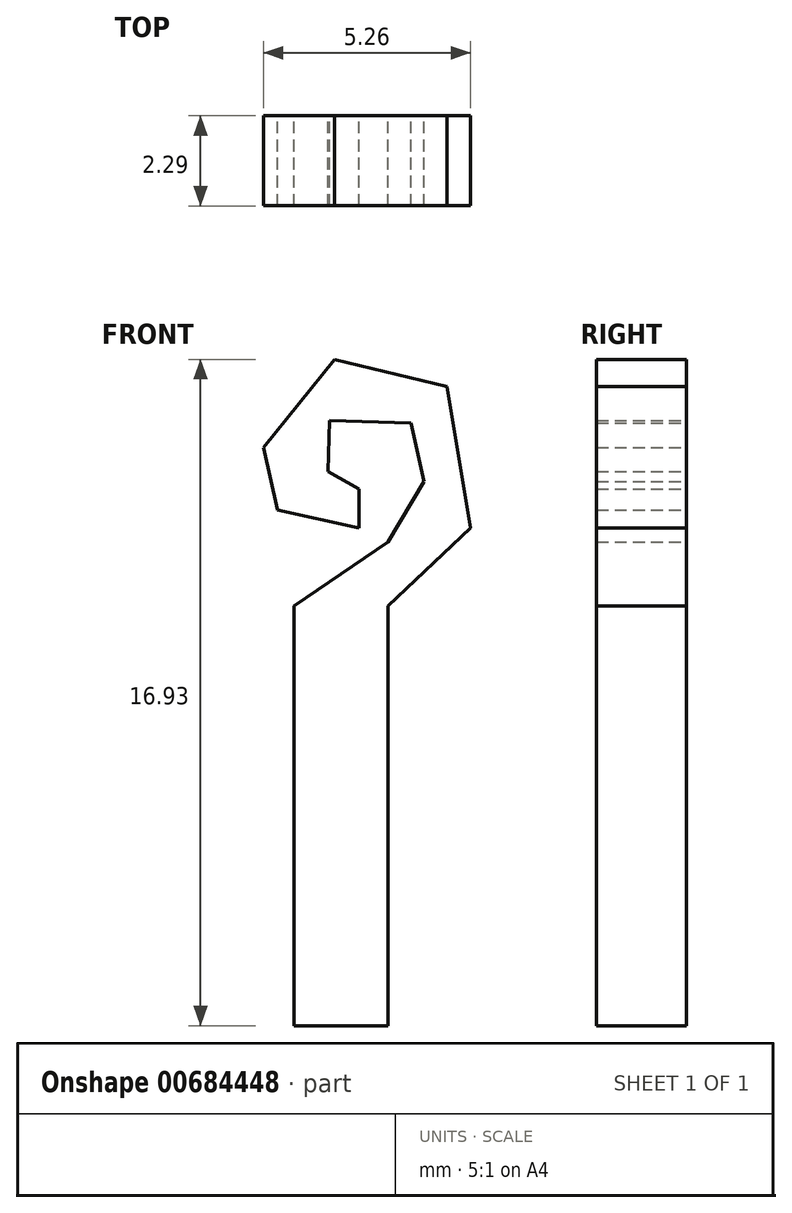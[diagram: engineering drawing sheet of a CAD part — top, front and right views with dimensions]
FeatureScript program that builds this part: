
annotation { "Feature Type Name" : "Feature", "Feature Type Description" : "" }
export const myFeature = defineFeature(function(context is Context, id is Id, definition is map)
    precondition{}
    {
        {
            var Q0;
            Q0=qCreatedBy(makeId("Front.planeOp"),FACE);
            var sketch = newSketch(context, id + "F0", { "sketchPlane" : qUnion([Q0])});
            skLineSegment(sketch, "E0", {"start": v(0, 0) * mm, "end": v(0, 10.67) * mm});
            skLineSegment(sketch, "E1", {"start": v(0, 0) * mm, "end": v(2.39, 0) * mm});
            skLineSegment(sketch, "E2", {"start": v(2.39, 0) * mm, "end": v(2.39, 10.67) * mm});
            skLineSegment(sketch, "E3", {"start": v(2.39, 10.67) * mm, "end": v(4.49, 12.65) * mm});
            skLineSegment(sketch, "E4", {"start": v(4.49, 12.65) * mm, "end": v(3.9, 16.23) * mm});
            skLineSegment(sketch, "E5", {"start": v(3.9, 16.23) * mm, "end": v(1.03, 16.93) * mm});
            skLineSegment(sketch, "E6", {"start": v(1.03, 16.93) * mm, "end": v(-0.77, 14.69) * mm});
            skLineSegment(sketch, "E7", {"start": v(-0.77, 14.69) * mm, "end": v(-0.41, 13.1) * mm});
            skLineSegment(sketch, "E8", {"start": v(-0.41, 13.1) * mm, "end": v(1.66, 12.65) * mm});
            skLineSegment(sketch, "E9", {"start": v(0, 10.67) * mm, "end": v(2.39, 12.29) * mm});
            skLineSegment(sketch, "E10", {"start": v(2.39, 12.29) * mm, "end": v(3.3, 13.83) * mm});
            skLineSegment(sketch, "E11", {"start": v(3.3, 13.83) * mm, "end": v(2.98, 15.31) * mm});
            skLineSegment(sketch, "E12", {"start": v(2.98, 15.31) * mm, "end": v(0.9, 15.37) * mm});
            skLineSegment(sketch, "E13", {"start": v(0.9, 15.37) * mm, "end": v(0.87, 14.09) * mm});
            skLineSegment(sketch, "E14", {"start": v(0.87, 14.09) * mm, "end": v(1.66, 13.64) * mm});
            skLineSegment(sketch, "E15", {"start": v(1.66, 13.64) * mm, "end": v(1.66, 12.65) * mm});
            skSolve(sketch);
        }
        {
            var Q0;
            Q0 = qSketchRegion(id + "F0", true);
            var Q1;
            Q1=makeQuery(id+"F0.imprint","IMPRINT",FACE,{"disambiguationData":[TD([[makeQuery(id+"F0.imprint","IMPRINT",EDGE,{"derivedFrom":sQuery(id+"F0.wireOp",EDGE,"E0")}),-1.0]])]});
            extrude(context, id + "F1", {"entities" : qUnion([Q0, Q1]), "depth" : 2.3 * mm, "offsetDistance" : 25.4 * mm});
        }
    });
